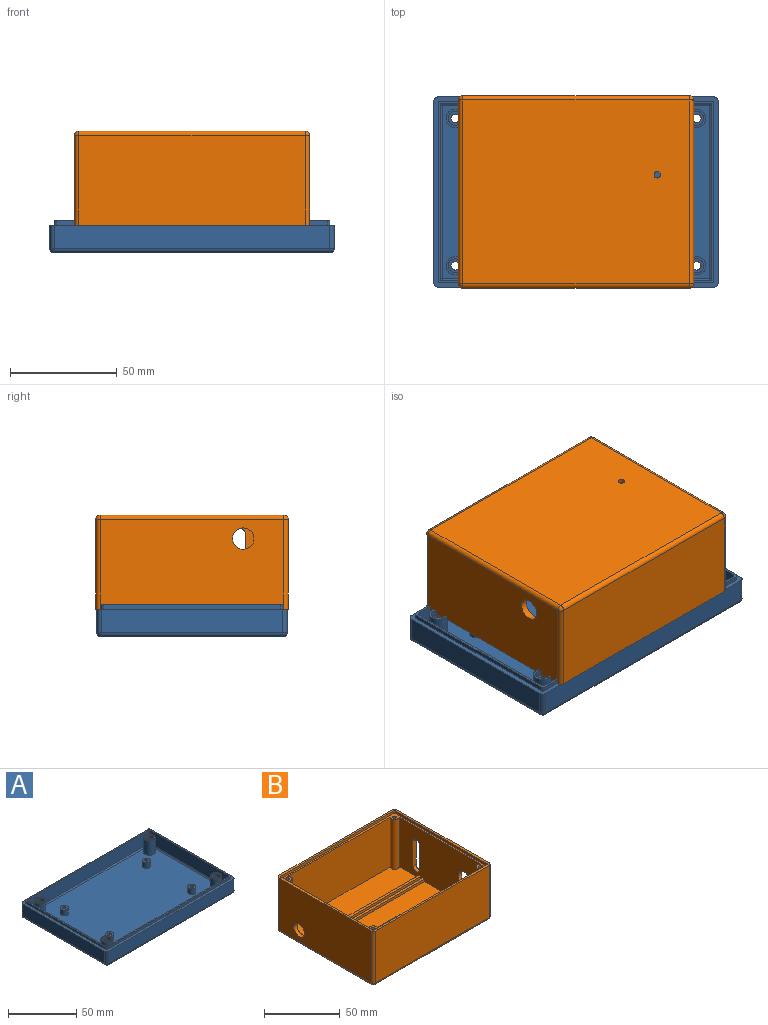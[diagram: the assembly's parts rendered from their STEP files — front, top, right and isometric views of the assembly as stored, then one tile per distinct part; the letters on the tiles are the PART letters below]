
ASSEMBLY  parts=2 mates=1
PART A: 88 faces, bbox 133x89x15 mm
  f0: plane 85x11mm, normal (1,0,0), area 935mm2, adj f5,f37,f41,f43
  f1: plane 129x11mm, normal (0,1,0), area 1419mm2, adj f5,f34,f40,f43
  f2: plane 85x11mm, normal (-1,0,0), area 935mm2, adj f5,f32,f34,f35
  f3: plane 129x11mm, normal (0,-1,0), area 1419mm2, adj f5,f32,f36,f37
  f4: plane 129x85mm, normal (0,0,-1), area 10851.9mm2, adj f35,f36,f40,f41,f76,f78,f80,f82
  f5: plane 133x89mm, normal (0,0,1), area 869.4mm2, adj f0,f1,f2,f3,f6,f7,f8,f9
  f6: plane 127x2mm, normal (0,1,0), area 254mm2, adj f5,f10,f44,f47
  f7: plane 83x2mm, normal (-1,0,0), area 166mm2, adj f5,f10,f44,f45
  f8: plane 127x2mm, normal (0,-1,0), area 254mm2, adj f5,f10,f45,f46
  f9: plane 83x2mm, normal (1,0,0), area 166mm2, adj f5,f10,f46,f47
  f10: plane 129x85mm, normal (0,0,1), area 424mm2, adj f6,f7,f8,f9,f12,f13,f14,f15
  f11: plane 125x81mm, normal (0,0,1), area 9784.9mm2, adj f17,f21,f25,f29,f53,f54,f57,f58
  f12: plane 125x12mm, normal (0,-1,0), area 1500mm2, adj f10,f50,f51,f54
  f13: plane 81x12mm, normal (1,0,0), area 972mm2, adj f10,f49,f50,f53
  f14: plane 125x12mm, normal (0,1,0), area 1500mm2, adj f10,f48,f49,f57
  f15: plane 81x12mm, normal (-1,0,0), area 972mm2, adj f10,f48,f51,f58
  f16: cylinder r=1.25mm len=5mm, axis (0,0,-1), area 39.3mm2, adj f18,f19
  f17: cylinder r=3mm len=6mm, axis (0,0,-1), area 94.2mm2, adj f11,f18
  f18: plane 6x6mm, normal (0,0,1), area 23.4mm2, adj f16,f17
  f19: plane 2.5x2.5mm, normal (0,0,1), area 4.9mm2, adj f16
  f20: cylinder r=1.25mm len=5mm, axis (0,0,-1), area 39.3mm2, adj f22,f23
  f21: cylinder r=3mm len=6mm, axis (0,0,-1), area 94.2mm2, adj f11,f22
  f22: plane 6x6mm, normal (0,0,1), area 23.4mm2, adj f20,f21
  f23: plane 2.5x2.5mm, normal (0,0,1), area 4.9mm2, adj f20
  f24: cylinder r=1.25mm len=5mm, axis (0,0,-1), area 39.3mm2, adj f26,f27
  f25: cylinder r=3mm len=6mm, axis (0,0,-1), area 94.2mm2, adj f11,f26
  f26: plane 6x6mm, normal (0,0,1), area 23.4mm2, adj f24,f25
  f27: plane 2.5x2.5mm, normal (0,0,1), area 4.9mm2, adj f24
  f28: cylinder r=1.25mm len=5mm, axis (0,0,-1), area 39.3mm2, adj f30,f31
  f29: cylinder r=3mm len=6mm, axis (0,0,-1), area 94.2mm2, adj f11,f30
  f30: plane 6x6mm, normal (0,0,1), area 23.4mm2, adj f28,f29
  f31: plane 2.5x2.5mm, normal (0,0,1), area 4.9mm2, adj f28
  f32: cylinder r=2mm len=11mm, axis (0,0,1), area 34.6mm2, adj f2,f3,f5,f33
  f33: sphere r=2mm, area 6.3mm2, adj f32,f35,f36
  f34: cylinder r=2mm len=11mm, axis (0,0,-1), area 34.6mm2, adj f1,f2,f5,f38
  f35: cylinder r=2mm len=85mm, axis (0,-1,0), area 267mm2, adj f2,f4,f33,f38
  f36: cylinder r=2mm len=129mm, axis (1,0,0), area 405.3mm2, adj f3,f4,f33,f39
  f37: cylinder r=2mm len=11mm, axis (0,0,-1), area 34.6mm2, adj f0,f3,f5,f39
  f38: sphere r=2mm, area 6.3mm2, adj f34,f35,f40
  f39: sphere r=2mm, area 6.3mm2, adj f36,f37,f41
  f40: cylinder r=2mm len=129mm, axis (-1,0,0), area 405.3mm2, adj f1,f4,f38,f42
  f41: cylinder r=2mm len=85mm, axis (0,1,0), area 267mm2, adj f0,f4,f39,f42
  f42: sphere r=2mm, area 6.3mm2, adj f40,f41,f43
  f43: cylinder r=2mm len=11mm, axis (0,0,1), area 34.6mm2, adj f0,f1,f5,f42
  f44: cylinder r=1mm len=2mm, axis (0,0,-1), area 3.1mm2, adj f5,f6,f7,f10
  f45: cylinder r=1mm len=2mm, axis (0,0,-1), area 3.1mm2, adj f5,f7,f8,f10
  f46: cylinder r=1mm len=2mm, axis (0,0,-1), area 3.1mm2, adj f5,f8,f9,f10
  f47: cylinder r=1mm len=2mm, axis (0,0,-1), area 3.1mm2, adj f5,f6,f9,f10
  f48: cylinder r=1mm len=12mm, axis (0,0,1), area 18.8mm2, adj f10,f14,f15,f59
  f49: cylinder r=1mm len=12mm, axis (0,0,1), area 18.8mm2, adj f10,f13,f14,f55
  f50: cylinder r=1mm len=12mm, axis (0,0,1), area 18.8mm2, adj f10,f12,f13,f52
  f51: cylinder r=1mm len=12mm, axis (0,0,1), area 18.8mm2, adj f10,f12,f15,f56
  f52: sphere r=1mm, area 1.6mm2, adj f50,f53,f54
  f53: cylinder r=1mm len=81mm, axis (0,1,0), area 127.2mm2, adj f11,f13,f52,f55
  f54: cylinder r=1mm len=125mm, axis (1,0,0), area 196.3mm2, adj f11,f12,f52,f56
  f55: sphere r=1mm, area 1.6mm2, adj f49,f53,f57
  f56: sphere r=1mm, area 1.6mm2, adj f51,f54,f58
  f57: cylinder r=1mm len=125mm, axis (-1,0,0), area 196.3mm2, adj f11,f14,f55,f59
  f58: cylinder r=1mm len=81mm, axis (0,-1,0), area 127.2mm2, adj f11,f15,f56,f59
  f59: sphere r=1mm, area 1.6mm2, adj f48,f57,f58
  f60: cylinder r=4.25mm len=13mm, axis (0,0,-1), area 347.1mm2, adj f11,f61
  f61: plane 8.5x8.5mm, normal (0,0,1), area 23.6mm2, adj f60,f74
  f62: cylinder r=4.25mm len=13mm, axis (0,0,-1), area 347.1mm2, adj f11,f63
  f63: plane 8.5x8.5mm, normal (0,0,1), area 23.6mm2, adj f62,f72
  f64: cylinder r=4.25mm len=13mm, axis (0,0,-1), area 347.1mm2, adj f11,f65
  f65: plane 8.5x8.5mm, normal (0,0,1), area 23.6mm2, adj f64,f70
  f66: cylinder r=4.25mm len=13mm, axis (0,0,-1), area 347.1mm2, adj f11,f67
  f67: plane 8.5x8.5mm, normal (0,0,1), area 23.6mm2, adj f66,f68
  f68: cylinder r=3.25mm len=6.5mm, axis (0,0,1), area 61.3mm2, adj f67,f69
  f69: plane 6.5x6.5mm, normal (0,0,1), area 20.6mm2, adj f68,f85
  f70: cylinder r=3.25mm len=6.5mm, axis (0,0,1), area 61.3mm2, adj f65,f71
  f71: plane 6.5x6.5mm, normal (0,0,1), area 20.6mm2, adj f70,f86
  f72: cylinder r=3.25mm len=6.5mm, axis (0,0,1), area 61.3mm2, adj f63,f73
  f73: plane 6.5x6.5mm, normal (0,0,1), area 20.6mm2, adj f72,f87
  f74: cylinder r=3.25mm len=6.5mm, axis (0,0,1), area 61.3mm2, adj f61,f75
  f75: plane 6.5x6.5mm, normal (0,0,1), area 20.6mm2, adj f74,f84
  f76: cylinder r=3mm len=11mm, axis (0,0,-1), area 207.3mm2, adj f4,f77
  f77: plane 6x6mm, normal (0,0,-1), area 15.7mm2, adj f76,f87
  f78: cylinder r=3mm len=11mm, axis (0,0,-1), area 207.3mm2, adj f4,f79
  f79: plane 6x6mm, normal (0,0,-1), area 15.7mm2, adj f78,f86
  f80: cylinder r=3mm len=11mm, axis (0,0,-1), area 207.3mm2, adj f4,f81
  f81: plane 6x6mm, normal (0,0,-1), area 15.7mm2, adj f80,f85
  f82: cylinder r=3mm len=11mm, axis (0,0,-1), area 207.3mm2, adj f4,f83
  f83: plane 6x6mm, normal (0,0,-1), area 15.7mm2, adj f82,f84
  f84: cylinder r=2mm len=4mm, axis (0,0,-1), area 12.6mm2, adj f75,f83
  f85: cylinder r=2mm len=4mm, axis (0,0,-1), area 12.6mm2, adj f69,f81
  f86: cylinder r=2mm len=4mm, axis (0,0,-1), area 12.6mm2, adj f71,f79
  f87: cylinder r=2mm len=4mm, axis (0,0,-1), area 12.6mm2, adj f73,f77
PART B: 67 faces, bbox 110x90x44 mm
  f0: plane 30x20.94mm, normal (0,0,1), area 628.1mm2, adj f60,f62,f63,f65
  f1: plane 104x2mm, normal (0,0,1), area 208mm2, adj f3,f6,f48,f50
  f2: plane 104x22mm, normal (0,0,1), area 2243.8mm2, adj f3,f4,f6,f19,f21,f47
  f3: plane 75.53x40mm, normal (1,0,0), area 2934.6mm2, adj f1,f2,f7,f8,f21,f22,f47,f48
  f4: plane 95.53x40mm, normal (0,-1,0), area 3821.1mm2, adj f2,f8,f19,f21
  f5: plane 95.53x40mm, normal (0,1,0), area 3821.1mm2, adj f7,f8,f20,f22
  f6: plane 75.53x40mm, normal (-1,0,0), area 2751.7mm2, adj f1,f2,f7,f8,f19,f20,f47,f48
  f7: plane 104x56mm, normal (0,0,1), area 4874.8mm2, adj f3,f5,f6,f20,f22,f51,f59,f60
  f8: plane 107x87mm, normal (0,0,1), area 640.9mm2, adj f3,f4,f5,f6,f9,f10,f11,f12
  f9: plane 85x2mm, normal (1,0,0), area 170mm2, adj f8,f13,f35,f38
  f10: plane 105x2mm, normal (0,-1,0), area 210mm2, adj f8,f13,f35,f36
  f11: plane 85x2mm, normal (-1,0,0), area 170mm2, adj f8,f13,f36,f37
  f12: plane 105x2mm, normal (0,1,0), area 210mm2, adj f8,f13,f37,f38
  f13: plane 110x90mm, normal (0,0,1), area 588.4mm2, adj f9,f10,f11,f12,f15,f16,f17,f18
  f14: plane 106x86mm, normal (0,0,-1), area 9108.9mm2, adj f26,f27,f31,f32,f59
  f15: plane 106x42mm, normal (0,-1,0), area 4452mm2, adj f13,f23,f27,f28
  f16: plane 86x42mm, normal (-1,0,0), area 3533.5mm2, adj f13,f23,f25,f26,f53
  f17: plane 106x42mm, normal (0,1,0), area 4452mm2, adj f13,f25,f31,f34
  f18: plane 86x42mm, normal (1,0,0), area 3350.6mm2, adj f13,f28,f32,f34,f54,f55,f56,f57
  f19: cylinder r=3mm len=40mm, axis (0,0,-1), area 363.6mm2, adj f2,f4,f6,f8
  f20: cylinder r=3mm len=40mm, axis (0,0,-1), area 363.6mm2, adj f5,f6,f7,f8
  f21: cylinder r=3mm len=40mm, axis (0,0,-1), area 363.6mm2, adj f2,f3,f4,f8
  f22: cylinder r=3mm len=40mm, axis (0,0,-1), area 363.6mm2, adj f3,f5,f7,f8
  f23: cylinder r=2mm len=42mm, axis (0,0,1), area 131.9mm2, adj f13,f15,f16,f24
  f24: sphere r=2mm, area 6.3mm2, adj f23,f26,f27
  f25: cylinder r=2mm len=42mm, axis (0,0,-1), area 131.9mm2, adj f13,f16,f17,f29
  f26: cylinder r=2mm len=86mm, axis (0,-1,0), area 270.2mm2, adj f14,f16,f24,f29
  f27: cylinder r=2mm len=106mm, axis (1,0,0), area 333mm2, adj f14,f15,f24,f30
  f28: cylinder r=2mm len=42mm, axis (0,0,-1), area 131.9mm2, adj f13,f15,f18,f30
  f29: sphere r=2mm, area 6.3mm2, adj f25,f26,f31
  f30: sphere r=2mm, area 6.3mm2, adj f27,f28,f32
  f31: cylinder r=2mm len=106mm, axis (-1,0,0), area 333mm2, adj f14,f17,f29,f33
  f32: cylinder r=2mm len=86mm, axis (0,1,0), area 270.2mm2, adj f14,f18,f30,f33
  f33: sphere r=2mm, area 6.3mm2, adj f31,f32,f34
  f34: cylinder r=2mm len=42mm, axis (0,0,1), area 131.9mm2, adj f13,f17,f18,f33
  f35: cylinder r=1mm len=2mm, axis (0,0,1), area 3.1mm2, adj f8,f9,f10,f13
  f36: cylinder r=1mm len=2mm, axis (0,0,-1), area 3.1mm2, adj f8,f10,f11,f13
  f37: cylinder r=1mm len=2mm, axis (0,0,1), area 3.1mm2, adj f8,f11,f12,f13
  f38: cylinder r=1mm len=2mm, axis (0,0,-1), area 3.1mm2, adj f8,f9,f12,f13
  f39: plane 2.5x2.5mm, normal (0,0,1), area 4.9mm2, adj f40
  f40: cylinder r=1.25mm len=40mm, axis (0,0,-1), area 314.2mm2, adj f8,f39
  f41: plane 2.5x2.5mm, normal (0,0,1), area 4.9mm2, adj f42
  f42: cylinder r=1.25mm len=40mm, axis (0,0,-1), area 314.2mm2, adj f8,f41
  f43: plane 2.5x2.5mm, normal (0,0,1), area 4.9mm2, adj f44
  f44: cylinder r=1.25mm len=40mm, axis (0,0,-1), area 314.2mm2, adj f8,f43
  f45: plane 2.5x2.5mm, normal (0,0,1), area 4.9mm2, adj f46
  f46: cylinder r=1.25mm len=40mm, axis (0,0,-1), area 314.2mm2, adj f8,f45
  f47: plane 104x2mm, normal (0,1,0), area 208mm2, adj f2,f3,f6,f49
  f48: plane 104x2mm, normal (0,-1,0), area 208mm2, adj f1,f3,f6,f49
  f49: plane 104x2mm, normal (0,0,1), area 208mm2, adj f3,f6,f47,f48
  f50: plane 104x2mm, normal (0,1,0), area 208mm2, adj f1,f3,f6,f52
  f51: plane 104x2mm, normal (0,-1,0), area 208mm2, adj f3,f6,f7,f52
  f52: plane 104x2mm, normal (0,0,1), area 208mm2, adj f3,f6,f50,f51
  f53: cylinder r=5mm len=10mm, axis (-1,0,0), area 94.2mm2, adj f3,f16
  f54: cylinder r=6mm len=12mm, axis (1,0,0), area 113.1mm2, adj f6,f18
  f55: cylinder r=3mm len=6mm, axis (1,0,0), area 28.3mm2, adj f6,f18,f56,f57
  f56: plane 20x3mm, normal (0,-1,0), area 60mm2, adj f6,f18,f55,f58
  f57: plane 20x3mm, normal (0,1,0), area 60mm2, adj f6,f18,f55,f58
  f58: cylinder r=3mm len=6mm, axis (1,0,0), area 28.3mm2, adj f6,f18,f56,f57
  f59: cylinder r=1.5mm len=3mm, axis (0,0,1), area 18.8mm2, adj f7,f14
  f60: plane 26.94x6mm, normal (1,0,0), area 143.6mm2, adj f0,f7,f62,f65
  f61: plane 29.94x9mm, normal (-1,0,0), area 228.9mm2, adj f7,f62,f64,f66
  f62: plane 33x9mm, normal (0,-1,0), area 207mm2, adj f0,f7,f60,f61,f63,f64
  f63: plane 29.94x9mm, normal (1,0,0), area 85.3mm2, adj f0,f7,f62,f64,f65,f66
  f64: plane 20.94x3mm, normal (0,0,1), area 62.8mm2, adj f61,f62,f63,f66
  f65: plane 30x6mm, normal (0,0.71,0.71), area 254.6mm2, adj f0,f7,f60,f63
  f66: plane 9x9mm, normal (0,0.71,0.71), area 38.2mm2, adj f7,f61,f63,f64
PLACE A t=(5.16,0.53,-11.18)mm fixed
PLACE B rot(axis=(1,0,0),180deg) t=(5.16,0.53,45.82)mm
MATE fastened B.f13 <-> A.f5  axis (0,0,-1) through (5.16,0.53,1.82)mm
